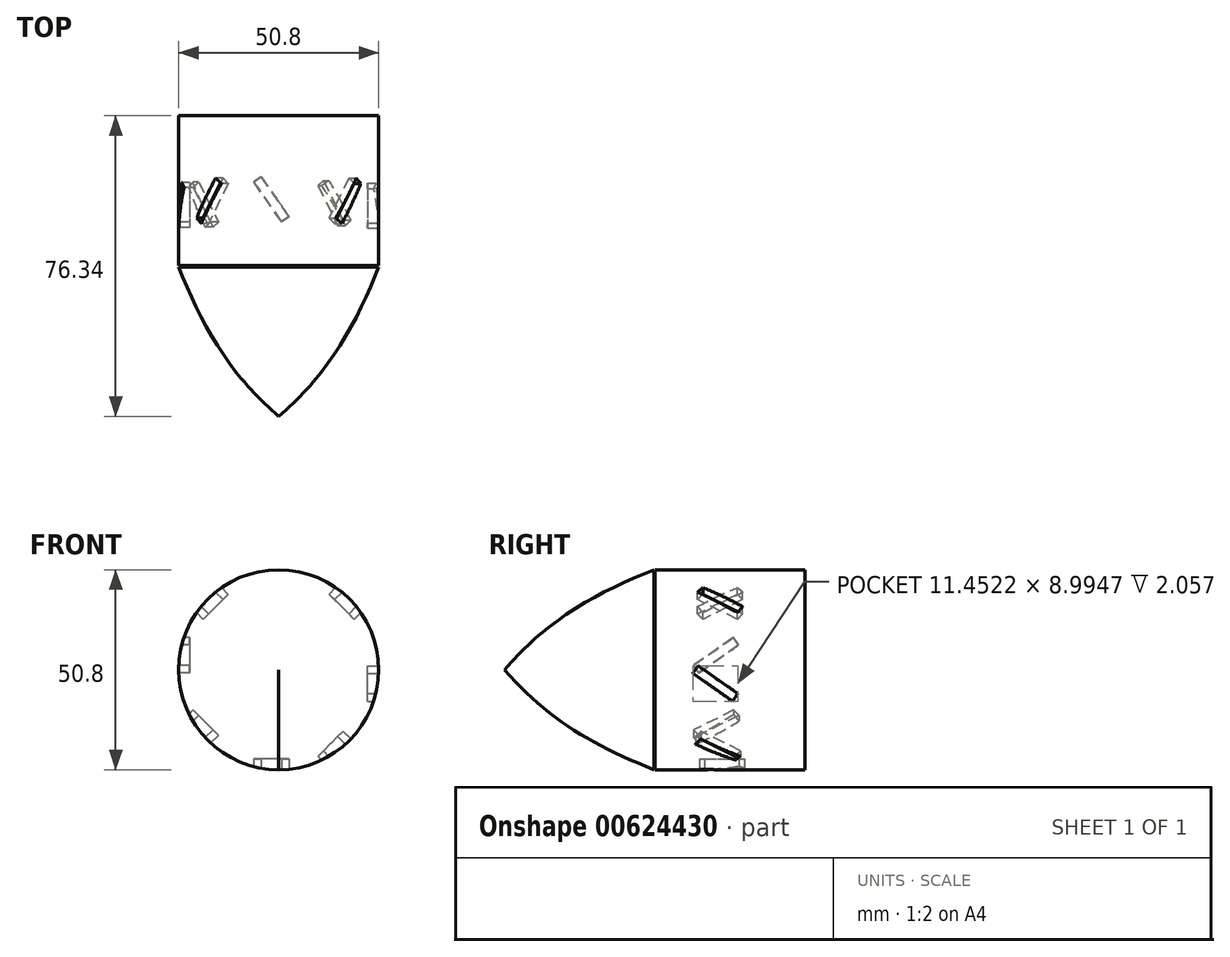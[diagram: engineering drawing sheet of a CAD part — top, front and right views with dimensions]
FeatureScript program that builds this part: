
annotation { "Feature Type Name" : "Feature", "Feature Type Description" : "" }
export const myFeature = defineFeature(function(context is Context, id is Id, definition is map)
    precondition{}
    {
        {
            var Q0;
            Q0=qCreatedBy(makeId("Front.planeOp"),FACE);
            var sketch = newSketch(context, id + "F0", { "sketchPlane" : qUnion([Q0])});
            skCircle(sketch, "E0", {"center": v(0, 0) * mm, "radius": 25.4 * mm});
            skSolve(sketch);
        }
        {
            var Q0;
            Q0=makeQuery(id+"F0.imprint","IMPRINT",FACE,{"disambiguationData":[TD([[makeQuery(id+"F0.imprint","IMPRINT",EDGE,{"derivedFrom":sQuery(id+"F0.wireOp",EDGE,"E0")}),1.0]])]});
            extrude(context, id + "F1", {"entities" : qUnion([Q0]), "depth" : 38.1 * mm, "offsetDistance" : 25.4 * mm});
        }
        {
            var Q0;
            Q0=qCreatedBy(makeId("Right.planeOp"),FACE);
            var sketch = newSketch(context, id + "F2", { "sketchPlane" : qUnion([Q0])});
            skLineSegment(sketch, "E1", {"start": v(-76.34, 0) * mm, "end": v(-38.37, 0) * mm});
            skLineSegment(sketch, "E2", {"start": v(-38.37, 0) * mm, "end": v(-38.37, 25.4) * mm});
            skLineSegment(sketch, "E3", {"start": v(-38.37, 0) * mm, "end": v(-38.37, -25.4) * mm});
            skFitSpline(sketch, "E4", {"points": [v(-38.37, -25.4) * mm, v(-76.34, 0) * mm], "startDerivative": vector(-48.65, 19.21) * mm, "endDerivative": vector(-31.18, 36.31) * mm});
            skSolve(sketch);
        }
        {
            var Q0;
            Q0=makeQuery(id+"F2.imprint","IMPRINT",FACE,{"disambiguationData":[TD([[makeQuery(id+"F2.imprint","IMPRINT",EDGE,{"derivedFrom":sQuery(id+"F2.wireOp",EDGE,"E1")}),-1.0]])]});
            var Q1;
            Q1=sQuery(id+"F2.wireOp",EDGE,"E1");
            revolve(context, id + "F3", {"entities" : qUnion([Q0]), "axis" : qUnion([Q1]), "revolveType" : RevolveType.FULL});
        }
        {
            var Q0;
            Q0=qCreatedBy(makeId("Right.planeOp"),FACE);
            cPlane(context, id + "F4", {"entities" : qUnion([Q0]), "cplaneType" : CPlaneType.OFFSET, "offset" : 25.4 * mm, "width" : 152.4 * mm, "height" : 152.4 * mm});
        }
        {
            var Q0;
            Q0=qCreatedBy(makeId("Right.planeOp"),FACE);
            cPlane(context, id + "F5", {"entities" : qUnion([Q0]), "cplaneType" : CPlaneType.OFFSET, "offset" : 25.4 * mm, "oppositeDirection" : true, "width" : 152.4 * mm, "height" : 152.4 * mm});
        }
        {
            var Q0;
            Q0=qCreatedBy(makeId("Top.planeOp"),FACE);
            cPlane(context, id + "F6", {"entities" : qUnion([Q0]), "cplaneType" : CPlaneType.OFFSET, "offset" : 25.4 * mm, "width" : 152.4 * mm, "height" : 152.4 * mm});
        }
        {
            var Q0;
            Q0=qCreatedBy(makeId("Top.planeOp"),FACE);
            cPlane(context, id + "F7", {"entities" : qUnion([Q0]), "cplaneType" : CPlaneType.OFFSET, "offset" : 25.4 * mm, "oppositeDirection" : true, "width" : 152.4 * mm, "height" : 152.4 * mm});
        }
        {
            var Q0;
            Q0=qCreatedBy(makeId("Right.planeOp"),FACE);
            var Q1;
            Q1=qCreatedBy(makeId("Top.planeOp"),FACE);
            cPlane(context, id + "F8", {"entities" : qUnion([Q0, Q1]), "cplaneType" : CPlaneType.MID_PLANE, "offset" : 25.4 * mm, "width" : 152.4 * mm, "height" : 152.4 * mm});
        }
        {
            var Q0;
            Q0=qCreatedBy(makeId("Right.planeOp"),FACE);
            var Q1;
            Q1=qCreatedBy(makeId("Top.planeOp"),FACE);
            cPlane(context, id + "F9", {"entities" : qUnion([Q0, Q1]), "cplaneType" : CPlaneType.MID_PLANE, "offset" : 25.4 * mm, "flipAlignment" : true, "width" : 152.4 * mm, "height" : 152.4 * mm});
        }
        {
            var Q0;
            Q0=qCreatedBy(id+"F8.planeOp",FACE);
            cPlane(context, id + "F10", {"entities" : qUnion([Q0]), "cplaneType" : CPlaneType.OFFSET, "offset" : 25.4 * mm, "width" : 152.4 * mm, "height" : 152.4 * mm});
        }
        {
            var Q0;
            Q0=qCreatedBy(id+"F8.planeOp",FACE);
            cPlane(context, id + "F11", {"entities" : qUnion([Q0]), "cplaneType" : CPlaneType.OFFSET, "offset" : 25.4 * mm, "oppositeDirection" : true, "width" : 152.4 * mm, "height" : 152.4 * mm});
        }
        {
            var Q0;
            Q0=qCreatedBy(id+"F9.planeOp",FACE);
            cPlane(context, id + "F12", {"entities" : qUnion([Q0]), "cplaneType" : CPlaneType.OFFSET, "offset" : 25.4 * mm, "width" : 152.4 * mm, "height" : 152.4 * mm});
        }
        {
            var Q0;
            Q0=qCreatedBy(id+"F9.planeOp",FACE);
            cPlane(context, id + "F13", {"entities" : qUnion([Q0]), "cplaneType" : CPlaneType.OFFSET, "offset" : 25.4 * mm, "oppositeDirection" : true, "width" : 152.4 * mm, "height" : 152.4 * mm});
        }
        {
            var Q0;
            Q0=qCreatedBy(id+"F12.planeOp",FACE);
            var sketch = newSketch(context, id + "F14", { "sketchPlane" : qUnion([Q0])});
            skLineSegment(sketch, "E5.bottom", {"start": v(-17.2, -4.5) * mm, "end": v(-27.32, 2.58) * mm});
            skLineSegment(sketch, "E5.top", {"start": v(-15.86, -2.58) * mm, "end": v(-25.98, 4.5) * mm});
            skLineSegment(sketch, "E5.left", {"start": v(-17.2, -4.5) * mm, "end": v(-15.86, -2.58) * mm});
            skLineSegment(sketch, "E5.right", {"start": v(-27.32, 2.58) * mm, "end": v(-25.98, 4.5) * mm});
            skPoint(sketch, "E5.middle", {"position": v(-21.59, 0) * mm});
            skLineSegment(sketch, "E6", {"start": v(-20.92, 0.96) * mm, "end": v(-22.26, -0.96) * mm});
            skLineSegment(sketch, "E7", {"start": v(-21.59, 0) * mm, "end": v(-12.75, 0) * mm});
            skLineSegment(sketch, "E8", {"start": v(-21.59, 0) * mm, "end": v(-16.53, -3.54) * mm});
            skLineSegment(sketch, "E9", {"start": v(-16.53, -3.54) * mm, "end": v(-14.32, -5.09) * mm});
            skSolve(sketch);
        }
        {
            var Q0;
            Q0=qCreatedBy(id+"F11.planeOp",FACE);
            var sketch = newSketch(context, id + "F15", { "sketchPlane" : qUnion([Q0])});
            skLineSegment(sketch, "E10.bottom", {"start": v(-15.86, 2.58) * mm, "end": v(-25.98, -4.5) * mm});
            skLineSegment(sketch, "E10.top", {"start": v(-17.2, 4.5) * mm, "end": v(-27.32, -2.58) * mm});
            skLineSegment(sketch, "E10.left", {"start": v(-15.86, 2.58) * mm, "end": v(-17.2, 4.5) * mm});
            skLineSegment(sketch, "E10.right", {"start": v(-25.98, -4.5) * mm, "end": v(-27.32, -2.58) * mm});
            skPoint(sketch, "E10.middle", {"position": v(-21.59, 0) * mm});
            skLineSegment(sketch, "E11", {"start": v(-20.92, -0.96) * mm, "end": v(-22.26, 0.96) * mm});
            skLineSegment(sketch, "E12", {"start": v(-21.59, 0) * mm, "end": v(-7.67, 0) * mm});
            skLineSegment(sketch, "E13", {"start": v(-21.6, 0) * mm, "end": v(-16.53, 3.54) * mm});
            skLineSegment(sketch, "E14", {"start": v(-16.53, 3.54) * mm, "end": v(-11.53, 7.05) * mm});
            skSolve(sketch);
        }
        {
            var Q0;
            Q0=qCreatedBy(id+"F5.planeOp",FACE);
            var sketch = newSketch(context, id + "F16", { "sketchPlane" : qUnion([Q0])});
            skLineSegment(sketch, "E15.bottom", {"start": v(-16.91, 6.26) * mm, "end": v(-27.03, -0.83) * mm});
            skLineSegment(sketch, "E15.top", {"start": v(-18.26, 8.17) * mm, "end": v(-28.37, 1.09) * mm});
            skLineSegment(sketch, "E15.left", {"start": v(-16.91, 6.26) * mm, "end": v(-18.26, 8.17) * mm});
            skLineSegment(sketch, "E15.right", {"start": v(-27.03, -0.83) * mm, "end": v(-28.37, 1.09) * mm});
            skPoint(sketch, "E15.middle", {"position": v(-22.64, 3.67) * mm});
            skLineSegment(sketch, "E16", {"start": v(-22.64, 3.67) * mm, "end": v(-6.1, 3.67) * mm});
            skLineSegment(sketch, "E17", {"start": v(-22.64, 3.67) * mm, "end": v(-17.58, 7.21) * mm});
            skLineSegment(sketch, "E18", {"start": v(-17.58, 7.21) * mm, "end": v(-13.37, 10.16) * mm});
            skSolve(sketch);
        }
        {
            var Q0;
            Q0=qCreatedBy(id+"F13.planeOp",FACE);
            var sketch = newSketch(context, id + "F17", { "sketchPlane" : qUnion([Q0])});
            skLineSegment(sketch, "E19.bottom", {"start": v(-16.86, 6.17) * mm, "end": v(-26.97, -0.9) * mm});
            skLineSegment(sketch, "E19.top", {"start": v(-18.2, 8.09) * mm, "end": v(-28.31, 1) * mm});
            skLineSegment(sketch, "E19.left", {"start": v(-16.86, 6.17) * mm, "end": v(-18.2, 8.09) * mm});
            skLineSegment(sketch, "E19.right", {"start": v(-26.97, -0.9) * mm, "end": v(-28.31, 1) * mm});
            skPoint(sketch, "E19.middle", {"position": v(-22.58, 3.6) * mm});
            skLineSegment(sketch, "E20", {"start": v(-22.58, 3.6) * mm, "end": v(-6.99, 3.6) * mm});
            skLineSegment(sketch, "E21", {"start": v(-22.58, 3.6) * mm, "end": v(-17.53, 7.13) * mm});
            skLineSegment(sketch, "E22", {"start": v(-17.53, 7.13) * mm, "end": v(-12.1, 10.94) * mm});
            skSolve(sketch);
        }
        {
            var Q0;
            Q0=qCreatedBy(id+"F7.planeOp",FACE);
            var sketch = newSketch(context, id + "F18", { "sketchPlane" : qUnion([Q0])});
            skLineSegment(sketch, "E23.bottom", {"start": v(0.7, -26.89) * mm, "end": v(-6.38, -16.78) * mm});
            skLineSegment(sketch, "E23.top", {"start": v(2.62, -25.55) * mm, "end": v(-4.46, -15.44) * mm});
            skLineSegment(sketch, "E23.left", {"start": v(0.7, -26.89) * mm, "end": v(2.62, -25.55) * mm});
            skLineSegment(sketch, "E23.right", {"start": v(-6.38, -16.78) * mm, "end": v(-4.46, -15.44) * mm});
            skPoint(sketch, "E23.middle", {"position": v(-1.88, -21.16) * mm});
            skLineSegment(sketch, "E24", {"start": v(-1.88, -21.16) * mm, "end": v(-1.88, -5.53) * mm});
            skLineSegment(sketch, "E25", {"start": v(-1.88, -21.16) * mm, "end": v(-5.42, -16.1) * mm});
            skLineSegment(sketch, "E26", {"start": v(-5.42, -16.1) * mm, "end": v(-9.93, -9.66) * mm});
            skSolve(sketch);
        }
        {
            var Q0;
            Q0=qCreatedBy(id+"F10.planeOp",FACE);
            var sketch = newSketch(context, id + "F19", { "sketchPlane" : qUnion([Q0])});
            skLineSegment(sketch, "E27.bottom", {"start": v(-17.75, -8.47) * mm, "end": v(-27.87, -1.39) * mm});
            skLineSegment(sketch, "E27.top", {"start": v(-16.41, -6.56) * mm, "end": v(-26.52, 0.53) * mm});
            skLineSegment(sketch, "E27.left", {"start": v(-17.75, -8.47) * mm, "end": v(-16.41, -6.56) * mm});
            skLineSegment(sketch, "E27.right", {"start": v(-27.87, -1.39) * mm, "end": v(-26.52, 0.53) * mm});
            skPoint(sketch, "E27.middle", {"position": v(-22.14, -3.97) * mm});
            skLineSegment(sketch, "E28", {"start": v(-22.14, -3.97) * mm, "end": v(-5.1, -3.97) * mm});
            skLineSegment(sketch, "E29", {"start": v(-22.14, -3.97) * mm, "end": v(-17.08, -7.51) * mm});
            skLineSegment(sketch, "E30", {"start": v(-17.08, -7.51) * mm, "end": v(-8.45, -13.56) * mm});
            skSolve(sketch);
        }
        {
            var Q0;
            Q0=qCreatedBy(id+"F4.planeOp",FACE);
            var sketch = newSketch(context, id + "F20", { "sketchPlane" : qUnion([Q0])});
            skLineSegment(sketch, "E31.bottom", {"start": v(-18.44, -7.99) * mm, "end": v(-28.55, -0.9) * mm});
            skLineSegment(sketch, "E31.top", {"start": v(-17.1, -6.07) * mm, "end": v(-27.21, 1) * mm});
            skLineSegment(sketch, "E31.left", {"start": v(-18.44, -7.99) * mm, "end": v(-17.1, -6.07) * mm});
            skLineSegment(sketch, "E31.right", {"start": v(-28.55, -0.9) * mm, "end": v(-27.21, 1) * mm});
            skPoint(sketch, "E31.middle", {"position": v(-22.83, -3.49) * mm});
            skLineSegment(sketch, "E32", {"start": v(-22.83, -3.49) * mm, "end": v(-5.32, -3.49) * mm});
            skLineSegment(sketch, "E33", {"start": v(-22.83, -3.49) * mm, "end": v(-21.42, -3.49) * mm});
            skLineSegment(sketch, "E34", {"start": v(-22.83, -3.49) * mm, "end": v(-17.77, -7.03) * mm});
            skLineSegment(sketch, "E35", {"start": v(-17.77, -7.03) * mm, "end": v(-8.11, -13.8) * mm});
            skSolve(sketch);
        }
        {
            var Q0;
            Q0 = qSketchRegion(id + "F14", true);
            extrude(context, id + "F21", {"entities" : qUnion([Q0]), "operationType" : NewBodyOperationType.REMOVE, "oppositeDirection" : true, "depth" : 2.8 * mm, "offsetDistance" : 25.4 * mm});
        }
        {
            var Q0;
            Q0 = qSketchRegion(id + "F20", true);
            extrude(context, id + "F22", {"entities" : qUnion([Q0]), "operationType" : NewBodyOperationType.REMOVE, "oppositeDirection" : true, "depth" : 2.8 * mm, "offsetDistance" : 25.4 * mm});
        }
        {
            var Q0;
            Q0 = qSketchRegion(id + "F19", true);
            extrude(context, id + "F23", {"entities" : qUnion([Q0]), "operationType" : NewBodyOperationType.REMOVE, "oppositeDirection" : true, "depth" : 2.8 * mm, "offsetDistance" : 25.4 * mm});
        }
        {
            var Q0;
            Q0 = qSketchRegion(id + "F18", true);
            extrude(context, id + "F24", {"entities" : qUnion([Q0]), "operationType" : NewBodyOperationType.REMOVE, "depth" : 2.8 * mm, "offsetDistance" : 25.4 * mm});
        }
        {
            var Q0;
            Q0 = qSketchRegion(id + "F17", true);
            extrude(context, id + "F25", {"entities" : qUnion([Q0]), "operationType" : NewBodyOperationType.REMOVE, "depth" : 2.8 * mm, "offsetDistance" : 25.4 * mm});
        }
        {
            var Q0;
            Q0 = qSketchRegion(id + "F16", true);
            extrude(context, id + "F26", {"entities" : qUnion([Q0]), "operationType" : NewBodyOperationType.REMOVE, "depth" : 2.8 * mm, "offsetDistance" : 25.4 * mm});
        }
        {
            var Q0;
            Q0 = qSketchRegion(id + "F15", true);
            extrude(context, id + "F27", {"entities" : qUnion([Q0]), "operationType" : NewBodyOperationType.REMOVE, "depth" : 2.8 * mm, "offsetDistance" : 25.4 * mm});
        }
    });
